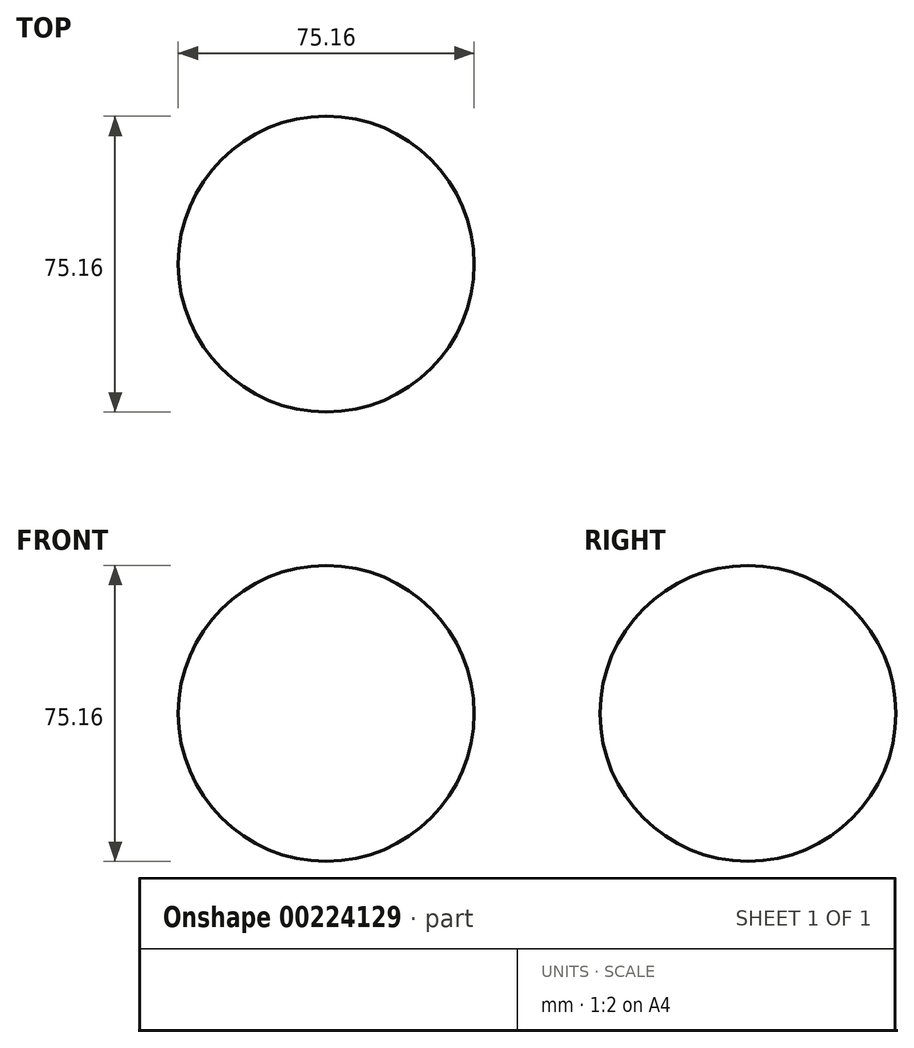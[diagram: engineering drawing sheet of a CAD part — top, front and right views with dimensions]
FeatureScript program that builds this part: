
annotation { "Feature Type Name" : "Feature", "Feature Type Description" : "" }
export const myFeature = defineFeature(function(context is Context, id is Id, definition is map)
    precondition{}
    {
        {
            var Q0;
            Q0=qCreatedBy(makeId("Front.planeOp"),FACE);
            var sketch = newSketch(context, id + "F0", { "sketchPlane" : qUnion([Q0])});
            skCircle(sketch, "E0", {"center": v(0, 0) * mm, "radius": 37.58 * mm});
            skLineSegment(sketch, "E1", {"start": v(0, 37.58) * mm, "end": v(0, -37.58) * mm});
            skSolve(sketch);
        }
        {
            var Q0;
            Q0=qCreatedBy(makeId("Front.planeOp"),FACE);
            var sketch = newSketch(context, id + "F1", { "sketchPlane" : qUnion([Q0])});
            skSolve(sketch);
        }
        {
            var Q0;
            Q0 = qSketchRegion(id + "F1", true);
            var Q1;
            {var subQ0=sQuery(id+"F0.wireOp",EDGE,"E1");Q1=makeQuery(id+"F0.imprint","IMPRINT",FACE,{"disambiguationData":[TD([[makeQuery(id+"F0.imprint","IMPRINT",EDGE,{"derivedFrom":subQ0}),-1.0]])]});}
            var Q2;
            Q2=sQuery(id+"F0.wireOp",EDGE,"E1");
            revolve(context, id + "F2", {"entities" : qUnion([Q0, Q1]), "axis" : qUnion([Q2]), "revolveType" : RevolveType.FULL});
        }
    });
